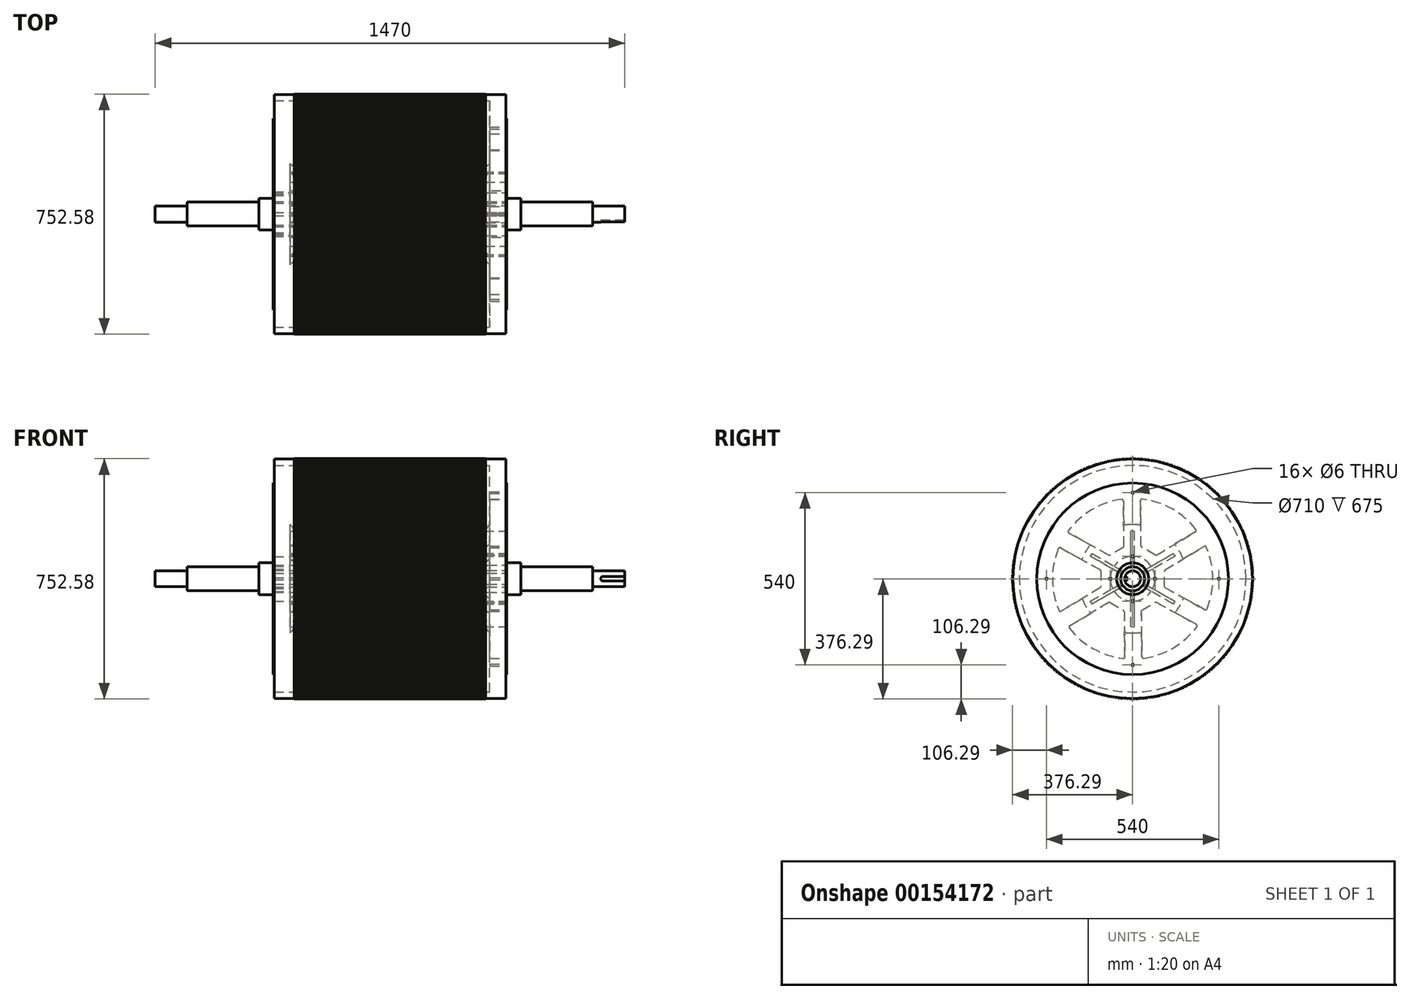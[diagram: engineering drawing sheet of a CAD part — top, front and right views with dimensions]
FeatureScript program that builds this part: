
annotation { "Feature Type Name" : "Feature", "Feature Type Description" : "" }
export const myFeature = defineFeature(function(context is Context, id is Id, definition is map)
    precondition{}
    {
        {
            var Q0;
            Q0=qCreatedBy(makeId("Front.planeOp"),FACE);
            var sketch = newSketch(context, id + "F0", { "sketchPlane" : qUnion([Q0])});
            skLineSegment(sketch, "E0", {"start": v(-128.4, 0) * mm, "end": v(171.6, 0) * mm, "construction": true});
            skLineSegment(sketch, "E1", {"start": v(0, 0) * mm, "end": v(362.5, 0) * mm});
            skLineSegment(sketch, "E2", {"start": v(0, 0) * mm, "end": v(-362.5, 0) * mm});
            skLineSegment(sketch, "E3", {"start": v(-362.5, 0) * mm, "end": v(-362.5, 375) * mm});
            skLineSegment(sketch, "E4", {"start": v(362.5, 375) * mm, "end": v(362.5, 0) * mm});
            skLineSegment(sketch, "E5.0", {"start": v(312.5, 355) * mm, "end": v(312.5, 70) * mm});
            skLineSegment(sketch, "E6", {"start": v(-312.5, 0) * mm, "end": v(-362.5, 0) * mm});
            skLineSegment(sketch, "E7", {"start": v(-362.5, 0) * mm, "end": v(-212.5, 0) * mm});
            skLineSegment(sketch, "E8", {"start": v(-212.5, 0) * mm, "end": v(-212.5, 70) * mm});
            skLineSegment(sketch, "E9", {"start": v(-212.5, 70) * mm, "end": v(-362.5, 70) * mm});
            skLineSegment(sketch, "E10.0", {"start": v(-212.5, 50) * mm, "end": v(-362.5, 50) * mm});
            skLineSegment(sketch, "E11", {"start": v(-362.5, 70) * mm, "end": v(-362.5, 50) * mm});
            skLineSegment(sketch, "E12", {"start": v(-212.5, 70) * mm, "end": v(-212.5, 50) * mm});
            skLineSegment(sketch, "E13", {"start": v(0, -51.64) * mm, "end": v(0, 29.66) * mm, "construction": true});
            skLineSegment(sketch, "E14", {"start": v(362.5, 0) * mm, "end": v(312.5, 0) * mm});
            skLineSegment(sketch, "E15", {"start": v(362.5, 0) * mm, "end": v(212.5, 0) * mm});
            skLineSegment(sketch, "E16", {"start": v(212.5, 0) * mm, "end": v(212.5, 70) * mm});
            skLineSegment(sketch, "E17", {"start": v(212.5, 70) * mm, "end": v(362.5, 70) * mm});
            skLineSegment(sketch, "E18.0", {"start": v(212.5, 50) * mm, "end": v(362.5, 50) * mm});
            skLineSegment(sketch, "E19", {"start": v(362.5, 70) * mm, "end": v(362.5, 50) * mm});
            skPoint(sketch, "E20", {"position": v(222.5, 170) * mm});
            skLineSegment(sketch, "E21", {"start": v(222.5, 170) * mm, "end": v(312.5, 170) * mm, "construction": true});
            skLineSegment(sketch, "E22", {"start": v(222.5, 170) * mm, "end": v(222.5, 70) * mm, "construction": true});
            skLineSegment(sketch, "E23", {"start": v(222.5, 70) * mm, "end": v(312.5, 170) * mm});
            skLineSegment(sketch, "E24.trimOffspring", {"start": v(-312.5, 70) * mm, "end": v(-312.5, 355) * mm});
            skPoint(sketch, "E25", {"position": v(-222.5, 170) * mm});
            skLineSegment(sketch, "E26", {"start": v(-222.5, 170) * mm, "end": v(-222.5, 70) * mm, "construction": true});
            skLineSegment(sketch, "E27", {"start": v(-222.5, 170) * mm, "end": v(-312.5, 170) * mm, "construction": true});
            skLineSegment(sketch, "E28", {"start": v(-222.5, 70) * mm, "end": v(-312.5, 170) * mm});
            skLineSegment(sketch, "E29", {"start": v(-362.5, 50) * mm, "end": v(-410, 50) * mm});
            skLineSegment(sketch, "E30", {"start": v(-410, 50) * mm, "end": v(-410, 42.5) * mm});
            skLineSegment(sketch, "E31", {"start": v(-410, 50) * mm, "end": v(-240, 50) * mm});
            skLineSegment(sketch, "E32", {"start": v(-240, 50) * mm, "end": v(-240, 0) * mm});
            skLineSegment(sketch, "E33", {"start": v(-410, 0) * mm, "end": v(-635, 0) * mm});
            skLineSegment(sketch, "E34", {"start": v(-362.5, 0) * mm, "end": v(-410, 0) * mm});
            skLineSegment(sketch, "E35", {"start": v(-635, 30) * mm, "end": v(-635, 37.5) * mm});
            skLineSegment(sketch, "E36", {"start": v(-635, 37.5) * mm, "end": v(-415, 37.5) * mm});
            skPoint(sketch, "E37.visualSharp", {"position": v(-410, 37.5) * mm});
            skArc(sketch, "E37.filletArc", {"start": v(-415, 37.5) * mm, "mid": v(-411.46, 38.96) * mm, "end": v(-410, 42.5) * mm});
            skLineSegment(sketch, "E38", {"start": v(362.5, 50) * mm, "end": v(410, 50) * mm});
            skLineSegment(sketch, "E39", {"start": v(410, 50) * mm, "end": v(410, 42.5) * mm});
            skLineSegment(sketch, "E40", {"start": v(410, 0) * mm, "end": v(362.5, 0) * mm});
            skLineSegment(sketch, "E41", {"start": v(410, 0) * mm, "end": v(635, 0) * mm});
            skLineSegment(sketch, "E42", {"start": v(635, 30) * mm, "end": v(635, 37.5) * mm});
            skLineSegment(sketch, "E43", {"start": v(635, 37.5) * mm, "end": v(415, 37.5) * mm});
            skPoint(sketch, "E44.visualSharp", {"position": v(410, 37.5) * mm});
            skArc(sketch, "E44.filletArc", {"start": v(410, 42.5) * mm, "mid": v(411.46, 38.96) * mm, "end": v(415, 37.5) * mm});
            skLineSegment(sketch, "E45", {"start": v(635, 0) * mm, "end": v(735, 0) * mm});
            skLineSegment(sketch, "E46", {"start": v(735, 0) * mm, "end": v(735, 25) * mm});
            skLineSegment(sketch, "E47", {"start": v(735, 25) * mm, "end": v(640, 25) * mm});
            skPoint(sketch, "E48.visualSharp", {"position": v(635, 25) * mm});
            skArc(sketch, "E48.filletArc", {"start": v(635, 30) * mm, "mid": v(636.46, 26.46) * mm, "end": v(640, 25) * mm});
            skLineSegment(sketch, "E49", {"start": v(735, 0) * mm, "end": v(660, 0) * mm});
            skLineSegment(sketch, "E50", {"start": v(660, 0) * mm, "end": v(660, 0) * mm});
            skLineSegment(sketch, "E51", {"start": v(-362.5, 50) * mm, "end": v(-362.5, 300) * mm});
            skLineSegment(sketch, "E52", {"start": v(-362.5, 300) * mm, "end": v(-365.5, 300) * mm});
            skLineSegment(sketch, "E53", {"start": v(-365.5, 300) * mm, "end": v(-365.5, 50) * mm});
            skLineSegment(sketch, "E54", {"start": v(362.5, 50) * mm, "end": v(362.5, 300) * mm});
            skLineSegment(sketch, "E55", {"start": v(362.5, 300) * mm, "end": v(365.5, 300) * mm});
            skLineSegment(sketch, "E56", {"start": v(365.5, 300) * mm, "end": v(365.5, 50) * mm});
            skLineSegment(sketch, "E57", {"start": v(-362.5, 375) * mm, "end": v(362.5, 375) * mm});
            skLineSegment(sketch, "E58.0", {"start": v(-362.5, 355) * mm, "end": v(362.5, 355) * mm});
            skLineSegment(sketch, "E59", {"start": v(-635, 0) * mm, "end": v(-735, 0) * mm});
            skLineSegment(sketch, "E60", {"start": v(-735, 0) * mm, "end": v(-735, 25) * mm});
            skLineSegment(sketch, "E61", {"start": v(-735, 25) * mm, "end": v(-640, 25) * mm});
            skPoint(sketch, "E62.visualSharp", {"position": v(-635, 25) * mm});
            skArc(sketch, "E62.filletArc", {"start": v(-640, 25) * mm, "mid": v(-636.46, 26.46) * mm, "end": v(-635, 30) * mm});
            skSolve(sketch);
        }
        {
            var Q0;
            {var subQ0=sQuery(id+"F0.wireOp",EDGE,"E30");Q0=makeQuery(id+"F0.imprint","IMPRINT",FACE,{"disambiguationData":[TD([[makeQuery(id+"F0.imprint","IMPRINT",EDGE,{"derivedFrom":subQ0}),1.0]])]});}
            var Q1;
            {var subQ0=sQuery(id+"F0.wireOp",EDGE,"E52");Q1=makeQuery(id+"F0.imprint","IMPRINT",FACE,{"disambiguationData":[TD([[makeQuery(id+"F0.imprint","IMPRINT",EDGE,{"derivedFrom":subQ0}),1.0]])]});}
            var Q2;
            {var subQ5=sQuery(id+"F0.wireOp",EDGE,"E32");Q2=makeQuery(id+"F0.imprint","IMPRINT",FACE,{"disambiguationData":[TD([[makeQuery(id+"F0.imprint","IMPRINT",EDGE,{"derivedFrom":subQ5}),-1.0]])]});}
            var Q3;
            {var subQ0=sQuery(id+"F0.wireOp",EDGE,"E8");Q3=makeQuery(id+"F0.imprint","IMPRINT",FACE,{"disambiguationData":[TD([[makeQuery(id+"F0.imprint","IMPRINT",EDGE,{"derivedFrom":subQ0}),1.0]])]});}
            var Q4;
            {var subQ0=sQuery(id+"F0.wireOp",EDGE,"E10.0");Q4=makeQuery(id+"F0.imprint","IMPRINT",FACE,{"disambiguationData":[TD([[makeQuery(id+"F0.imprint","IMPRINT",EDGE,{"derivedFrom":subQ0}),-1.0]])]});}
            var Q5;
            {var subQ3=sQuery(id+"F0.wireOp",EDGE,"E28");Q5=makeQuery(id+"F0.imprint","IMPRINT",FACE,{"disambiguationData":[TD([[makeQuery(id+"F0.imprint","IMPRINT",EDGE,{"derivedFrom":subQ3}),1.0]])]});}
            var Q6;
            {var subQ1=sQuery(id+"F0.wireOp",EDGE,"E9");var subQ4=sQuery(id+"F0.wireOp",EDGE,"E51");var subQ5=makeQuery(id+"F0.imprint","INTERSECT",VERTEX,{"derivedFrom":[subQ1,subQ4]});Q6=makeQuery(id+"F0.imprint","IMPRINT",FACE,{"disambiguationData":[TD([[makeQuery(id+"F0.imprint","IMPRINT",EDGE,{"disambiguationData":[TD([[subQ5,1.0]])],"derivedFrom":subQ1}),-1.0]])]});}
            var Q7;
            {var subQ4=sQuery(id+"F0.wireOp",EDGE,"E57");Q7=makeQuery(id+"F0.imprint","IMPRINT",FACE,{"disambiguationData":[TD([[makeQuery(id+"F0.imprint","IMPRINT",EDGE,{"derivedFrom":subQ4}),-1.0]])]});}
            var Q8;
            {var subQ1=sQuery(id+"F0.wireOp",EDGE,"E5.0");var subQ6=sQuery(id+"F0.wireOp",EDGE,"E58.0");var subQ7=makeQuery(id+"F0.imprint","INTERSECT",VERTEX,{"derivedFrom":[subQ1,subQ6]});Q8=makeQuery(id+"F0.imprint","IMPRINT",FACE,{"disambiguationData":[TD([[makeQuery(id+"F0.imprint","IMPRINT",EDGE,{"disambiguationData":[TD([[subQ7,-1.0]])],"derivedFrom":subQ1}),1.0]])]});}
            var Q9;
            {var subQ3=sQuery(id+"F0.wireOp",EDGE,"E23");Q9=makeQuery(id+"F0.imprint","IMPRINT",FACE,{"disambiguationData":[TD([[makeQuery(id+"F0.imprint","IMPRINT",EDGE,{"derivedFrom":subQ3}),-1.0]])]});}
            var Q10;
            {var subQ3=sQuery(id+"F0.wireOp",EDGE,"E18.0");Q10=makeQuery(id+"F0.imprint","IMPRINT",FACE,{"disambiguationData":[TD([[makeQuery(id+"F0.imprint","IMPRINT",EDGE,{"derivedFrom":subQ3}),-1.0]])]});}
            var Q11;
            {var subQ7=sQuery(id+"F0.wireOp",EDGE,"E18.0");Q11=makeQuery(id+"F0.imprint","IMPRINT",FACE,{"disambiguationData":[TD([[makeQuery(id+"F0.imprint","IMPRINT",EDGE,{"derivedFrom":subQ7}),1.0]])]});}
            var Q12;
            {var subQ4=sQuery(id+"F0.wireOp",EDGE,"E39");Q12=makeQuery(id+"F0.imprint","IMPRINT",FACE,{"disambiguationData":[TD([[makeQuery(id+"F0.imprint","IMPRINT",EDGE,{"derivedFrom":subQ4}),-1.0]])]});}
            var Q13;
            {var subQ0=sQuery(id+"F0.wireOp",EDGE,"E55");Q13=makeQuery(id+"F0.imprint","IMPRINT",FACE,{"disambiguationData":[TD([[makeQuery(id+"F0.imprint","IMPRINT",EDGE,{"derivedFrom":subQ0}),-1.0]])]});}
            var Q14;
            Q14=sQuery(id+"F0.wireOp",EDGE,"E2");
            revolve(context, id + "F1", {"entities" : qUnion([Q0, Q1, Q2, Q3, Q4, Q5, Q6, Q7, Q8, Q9, Q10, Q11, Q12, Q13]), "axis" : qUnion([Q14]), "revolveType" : RevolveType.FULL});
        }
        {
            var Q0;
            Q0=qCreatedBy(makeId("Right.planeOp"),FACE);
            cPlane(context, id + "F2", {"entities" : qUnion([Q0]), "cplaneType" : CPlaneType.OFFSET, "offset" : 362.5 * mm, "width" : 150 * mm, "height" : 150 * mm});
        }
        {
            var Q0;
            Q0=qCreatedBy(id+"F2.planeOp",FACE);
            var sketch = newSketch(context, id + "F3", { "sketchPlane" : qUnion([Q0])});
            skLineSegment(sketch, "E63", {"start": v(0, 0) * mm, "end": v(100, 0) * mm});
            skLineSegment(sketch, "E64", {"start": v(100, 0) * mm, "end": v(100, 24.17) * mm});
            skLineSegment(sketch, "E65", {"start": v(100, 0) * mm, "end": v(100, -24.06) * mm});
            skLineSegment(sketch, "E66", {"start": v(102.43, 28.46) * mm, "end": v(223.77, 101.26) * mm});
            skLineSegment(sketch, "E67", {"start": v(102.57, -28.43) * mm, "end": v(225.8, -96.84) * mm});
            skArc(sketch, "E68", {"start": v(230.94, 98.94) * mm, "mid": v(251.23, 2.49) * mm, "end": v(232.85, -94.34) * mm});
            skPoint(sketch, "E69.visualSharp", {"position": v(228.63, 104.17) * mm});
            skArc(sketch, "E69.filletArc", {"start": v(230.94, 98.94) * mm, "mid": v(227.88, 101.73) * mm, "end": v(223.77, 101.26) * mm});
            skPoint(sketch, "E70.newPointA", {"position": v(231.14, -99.8) * mm});
            skArc(sketch, "E70.filletArc", {"start": v(225.8, -96.84) * mm, "mid": v(229.88, -97.18) * mm, "end": v(232.85, -94.34) * mm});
            skPoint(sketch, "E71.visualSharp", {"position": v(100, 27) * mm});
            skArc(sketch, "E71.filletArc", {"start": v(102.43, 28.46) * mm, "mid": v(100.65, 26.63) * mm, "end": v(100, 24.17) * mm});
            skPoint(sketch, "E72.visualSharp", {"position": v(100, -27) * mm});
            skArc(sketch, "E72.filletArc", {"start": v(100, -24.06) * mm, "mid": v(100.7, -26.6) * mm, "end": v(102.57, -28.43) * mm});
            skArc(sketch, "E73.1.0", {"start": v(29.79, 249.47) * mm, "mid": v(123.46, 218.81) * mm, "end": v(198.13, 154.48) * mm});
            skArc(sketch, "E73.1.1", {"start": v(29.79, 249.47) * mm, "mid": v(25.84, 248.21) * mm, "end": v(24.2, 244.42) * mm});
            skLineSegment(sketch, "E73.1.2", {"start": v(26.57, 102.93) * mm, "end": v(24.2, 244.42) * mm});
            skLineSegment(sketch, "E73.1.3", {"start": v(50, 86.6) * mm, "end": v(29.07, 98.69) * mm});
            skArc(sketch, "E73.1.4", {"start": v(26.57, 102.93) * mm, "mid": v(27.26, 100.48) * mm, "end": v(29.07, 98.69) * mm});
            skLineSegment(sketch, "E73.1.5", {"start": v(50, 86.6) * mm, "end": v(70.83, 74.57) * mm});
            skArc(sketch, "E73.1.6", {"start": v(70.83, 74.57) * mm, "mid": v(73.38, 73.9) * mm, "end": v(75.9, 74.62) * mm});
            skLineSegment(sketch, "E73.1.7", {"start": v(75.9, 74.62) * mm, "end": v(196.76, 147.12) * mm});
            skArc(sketch, "E73.1.8", {"start": v(196.76, 147.12) * mm, "mid": v(199.1, 150.5) * mm, "end": v(198.13, 154.48) * mm});
            skArc(sketch, "E73.2.0", {"start": v(-201.15, 150.53) * mm, "mid": v(-127.77, 216.33) * mm, "end": v(-34.72, 248.83) * mm});
            skArc(sketch, "E73.2.1", {"start": v(-201.15, 150.53) * mm, "mid": v(-202.04, 146.49) * mm, "end": v(-199.58, 143.16) * mm});
            skLineSegment(sketch, "E73.2.2", {"start": v(-75.86, 74.48) * mm, "end": v(-199.58, 143.16) * mm});
            skLineSegment(sketch, "E73.2.3", {"start": v(-50, 86.6) * mm, "end": v(-70.93, 74.52) * mm});
            skArc(sketch, "E73.2.4", {"start": v(-75.86, 74.48) * mm, "mid": v(-73.39, 73.85) * mm, "end": v(-70.93, 74.52) * mm});
            skLineSegment(sketch, "E73.2.5", {"start": v(-50, 86.6) * mm, "end": v(-29.17, 98.63) * mm});
            skArc(sketch, "E73.2.6", {"start": v(-29.17, 98.63) * mm, "mid": v(-27.32, 100.5) * mm, "end": v(-26.67, 103.05) * mm});
            skLineSegment(sketch, "E73.2.7", {"start": v(-26.67, 103.05) * mm, "end": v(-29.03, 243.96) * mm});
            skArc(sketch, "E73.2.8", {"start": v(-29.03, 243.96) * mm, "mid": v(-30.78, 247.68) * mm, "end": v(-34.72, 248.83) * mm});
            skArc(sketch, "E73.3.0", {"start": v(-230.94, -98.94) * mm, "mid": v(-251.23, -2.49) * mm, "end": v(-232.85, 94.34) * mm});
            skArc(sketch, "E73.3.1", {"start": v(-230.94, -98.94) * mm, "mid": v(-227.88, -101.73) * mm, "end": v(-223.77, -101.26) * mm});
            skLineSegment(sketch, "E73.3.2", {"start": v(-102.43, -28.46) * mm, "end": v(-223.77, -101.26) * mm});
            skLineSegment(sketch, "E73.3.3", {"start": v(-100, 0) * mm, "end": v(-100, -24.17) * mm});
            skArc(sketch, "E73.3.4", {"start": v(-102.43, -28.46) * mm, "mid": v(-100.65, -26.63) * mm, "end": v(-100, -24.17) * mm});
            skLineSegment(sketch, "E73.3.5", {"start": v(-100, 0) * mm, "end": v(-100, 24.06) * mm});
            skArc(sketch, "E73.3.6", {"start": v(-100, 24.06) * mm, "mid": v(-100.7, 26.6) * mm, "end": v(-102.57, 28.43) * mm});
            skLineSegment(sketch, "E73.3.7", {"start": v(-102.57, 28.43) * mm, "end": v(-225.8, 96.84) * mm});
            skArc(sketch, "E73.3.8", {"start": v(-225.8, 96.84) * mm, "mid": v(-229.88, 97.18) * mm, "end": v(-232.85, 94.34) * mm});
            skArc(sketch, "E73.4.0", {"start": v(-29.79, -249.47) * mm, "mid": v(-123.46, -218.81) * mm, "end": v(-198.13, -154.48) * mm});
            skArc(sketch, "E73.4.1", {"start": v(-29.79, -249.47) * mm, "mid": v(-25.84, -248.21) * mm, "end": v(-24.2, -244.42) * mm});
            skLineSegment(sketch, "E73.4.2", {"start": v(-26.57, -102.93) * mm, "end": v(-24.2, -244.42) * mm});
            skLineSegment(sketch, "E73.4.3", {"start": v(-50, -86.6) * mm, "end": v(-29.07, -98.69) * mm});
            skArc(sketch, "E73.4.4", {"start": v(-26.57, -102.93) * mm, "mid": v(-27.26, -100.48) * mm, "end": v(-29.07, -98.69) * mm});
            skLineSegment(sketch, "E73.4.5", {"start": v(-50, -86.6) * mm, "end": v(-70.83, -74.57) * mm});
            skArc(sketch, "E73.4.6", {"start": v(-70.83, -74.57) * mm, "mid": v(-73.38, -73.9) * mm, "end": v(-75.9, -74.62) * mm});
            skLineSegment(sketch, "E73.4.7", {"start": v(-75.9, -74.62) * mm, "end": v(-196.76, -147.12) * mm});
            skArc(sketch, "E73.4.8", {"start": v(-196.76, -147.12) * mm, "mid": v(-199.1, -150.5) * mm, "end": v(-198.13, -154.48) * mm});
            skArc(sketch, "E73.5.0", {"start": v(201.15, -150.53) * mm, "mid": v(127.77, -216.33) * mm, "end": v(34.72, -248.83) * mm});
            skArc(sketch, "E73.5.1", {"start": v(201.15, -150.53) * mm, "mid": v(202.04, -146.49) * mm, "end": v(199.58, -143.16) * mm});
            skLineSegment(sketch, "E73.5.2", {"start": v(75.86, -74.48) * mm, "end": v(199.58, -143.16) * mm});
            skLineSegment(sketch, "E73.5.3", {"start": v(50, -86.6) * mm, "end": v(70.93, -74.52) * mm});
            skArc(sketch, "E73.5.4", {"start": v(75.86, -74.48) * mm, "mid": v(73.39, -73.85) * mm, "end": v(70.93, -74.52) * mm});
            skLineSegment(sketch, "E73.5.5", {"start": v(50, -86.6) * mm, "end": v(29.17, -98.63) * mm});
            skArc(sketch, "E73.5.6", {"start": v(29.17, -98.63) * mm, "mid": v(27.32, -100.5) * mm, "end": v(26.67, -103.05) * mm});
            skLineSegment(sketch, "E73.5.7", {"start": v(26.67, -103.05) * mm, "end": v(29.03, -243.96) * mm});
            skArc(sketch, "E73.5.8", {"start": v(29.03, -243.96) * mm, "mid": v(30.78, -247.68) * mm, "end": v(34.72, -248.83) * mm});
            skLineSegment(sketch, "E74", {"start": v(0, 0) * mm, "end": v(0, 150) * mm});
            skLineSegment(sketch, "E75", {"start": v(0, 150) * mm, "end": v(-5, 149.92) * mm});
            skLineSegment(sketch, "E76", {"start": v(0, 150) * mm, "end": v(5, 149.96) * mm});
            skPoint(sketch, "E76.endSnap0", {"position": v(-2.5, 149.96) * mm});
            skLineSegment(sketch, "E77", {"start": v(0, 0) * mm, "end": v(0, 42.5) * mm});
            skLineSegment(sketch, "E78", {"start": v(5, 149.96) * mm, "end": v(5, 42.5) * mm});
            skLineSegment(sketch, "E79", {"start": v(5, 42.5) * mm, "end": v(-5, 42.5) * mm});
            skLineSegment(sketch, "E80", {"start": v(-5, 42.5) * mm, "end": v(-5, 149.92) * mm});
            skLineSegment(sketch, "E81.1.0", {"start": v(-127.37, 79.3) * mm, "end": v(-34.3, 25.58) * mm});
            skLineSegment(sketch, "E81.1.1", {"start": v(-39.3, 16.92) * mm, "end": v(-132.33, 70.63) * mm});
            skLineSegment(sketch, "E81.1.2", {"start": v(-129.9, 75) * mm, "end": v(-127.37, 79.3) * mm});
            skLineSegment(sketch, "E81.1.3", {"start": v(-129.9, 75) * mm, "end": v(-132.33, 70.63) * mm});
            skLineSegment(sketch, "E81.1.4", {"start": v(-34.3, 25.58) * mm, "end": v(-39.3, 16.92) * mm});
            skLineSegment(sketch, "E81.2.0", {"start": v(-132.37, -70.65) * mm, "end": v(-39.3, -16.92) * mm});
            skLineSegment(sketch, "E81.2.1", {"start": v(-34.3, -25.58) * mm, "end": v(-127.33, -79.29) * mm});
            skLineSegment(sketch, "E81.2.2", {"start": v(-129.9, -75) * mm, "end": v(-132.37, -70.65) * mm});
            skLineSegment(sketch, "E81.2.3", {"start": v(-129.9, -75) * mm, "end": v(-127.33, -79.29) * mm});
            skLineSegment(sketch, "E81.2.4", {"start": v(-39.3, -16.92) * mm, "end": v(-34.3, -25.58) * mm});
            skLineSegment(sketch, "E81.3.0", {"start": v(-5, -149.96) * mm, "end": v(-5, -42.5) * mm});
            skLineSegment(sketch, "E81.3.1", {"start": v(5, -42.5) * mm, "end": v(5, -149.92) * mm});
            skLineSegment(sketch, "E81.3.2", {"start": v(0, -150) * mm, "end": v(-5, -149.96) * mm});
            skLineSegment(sketch, "E81.3.3", {"start": v(0, -150) * mm, "end": v(5, -149.92) * mm});
            skLineSegment(sketch, "E81.3.4", {"start": v(-5, -42.5) * mm, "end": v(5, -42.5) * mm});
            skLineSegment(sketch, "E81.4.0", {"start": v(127.37, -79.3) * mm, "end": v(34.3, -25.58) * mm});
            skLineSegment(sketch, "E81.4.1", {"start": v(39.3, -16.92) * mm, "end": v(132.33, -70.63) * mm});
            skLineSegment(sketch, "E81.4.2", {"start": v(129.9, -75) * mm, "end": v(127.37, -79.3) * mm});
            skLineSegment(sketch, "E81.4.3", {"start": v(129.9, -75) * mm, "end": v(132.33, -70.63) * mm});
            skLineSegment(sketch, "E81.4.4", {"start": v(34.3, -25.58) * mm, "end": v(39.3, -16.92) * mm});
            skLineSegment(sketch, "E81.5.0", {"start": v(132.37, 70.65) * mm, "end": v(39.3, 16.92) * mm});
            skLineSegment(sketch, "E81.5.1", {"start": v(34.3, 25.58) * mm, "end": v(127.33, 79.29) * mm});
            skLineSegment(sketch, "E81.5.2", {"start": v(129.9, 75) * mm, "end": v(132.37, 70.65) * mm});
            skLineSegment(sketch, "E81.5.3", {"start": v(129.9, 75) * mm, "end": v(127.33, 79.29) * mm});
            skLineSegment(sketch, "E81.5.4", {"start": v(39.3, 16.92) * mm, "end": v(34.3, 25.58) * mm});
            skSolve(sketch);
        }
        {
            var Q0;
            Q0=qSketchRegion(id+"F3",true);
            extrude(context, id + "F4", {"entities" : qUnion([Q0]), "operationType" : NewBodyOperationType.REMOVE, "oppositeDirection" : true, "depth" : 725 * mm});
        }
        {
            var Q0;
            Q0=qCreatedBy(makeId("Front.planeOp"),FACE);
            cPlane(context, id + "F5", {"entities" : qUnion([Q0]), "cplaneType" : CPlaneType.OFFSET, "offset" : 25 * mm, "width" : 150 * mm, "height" : 150 * mm});
        }
        {
            var Q0;
            Q0=qCreatedBy(id+"F5.planeOp",FACE);
            var sketch = newSketch(context, id + "F6", { "sketchPlane" : qUnion([Q0])});
            skLineSegment(sketch, "E82.0", {"start": v(735, -25) * mm, "end": v(735, 25) * mm});
            skLineSegment(sketch, "E83", {"start": v(735, -25) * mm, "end": v(735, 0) * mm});
            skLineSegment(sketch, "E84", {"start": v(735, 0) * mm, "end": v(697.5, 0) * mm});
            skLineSegment(sketch, "E85.left", {"start": v(735, 7) * mm, "end": v(735, -7) * mm});
            skPoint(sketch, "E85.middle", {"position": v(697.5, 0) * mm});
            skLineSegment(sketch, "E86.bottom", {"start": v(735, 7) * mm, "end": v(667, 7) * mm});
            skLineSegment(sketch, "E86.top", {"start": v(735, -7) * mm, "end": v(667, -7) * mm});
            skLineSegment(sketch, "E86.right", {"start": v(660, 0) * mm, "end": v(660, 0) * mm});
            skPoint(sketch, "E87.visualSharp", {"position": v(660, 7) * mm});
            skArc(sketch, "E87.filletArc", {"start": v(667, 7) * mm, "mid": v(662.05, 4.95) * mm, "end": v(660, 0) * mm});
            skPoint(sketch, "E88.visualSharp", {"position": v(660, -7) * mm});
            skArc(sketch, "E88.filletArc", {"start": v(660, 0) * mm, "mid": v(662.05, -4.95) * mm, "end": v(667, -7) * mm});
            skSolve(sketch);
        }
        {
            var Q0;
            Q0=qSketchRegion(id+"F6",true);
            extrude(context, id + "F7", {"entities" : qUnion([Q0]), "operationType" : NewBodyOperationType.REMOVE, "oppositeDirection" : true, "depth" : 6.5 * mm});
        }
        {
            var Q0;
            Q0=qCreatedBy(makeId("Right.planeOp"),FACE);
            cPlane(context, id + "F8", {"entities" : qUnion([Q0]), "cplaneType" : CPlaneType.OFFSET, "offset" : 300 * mm, "width" : 150 * mm, "height" : 150 * mm});
        }
        {
            var Q0;
            Q0=qCreatedBy(id+"F8.planeOp",FACE);
            var sketch = newSketch(context, id + "F9", { "sketchPlane" : qUnion([Q0])});
            skArc(sketch, "E89.0", {"start": v(-29.98, 373.8) * mm, "mid": v(-30.58, 373.75) * mm, "end": v(-31.18, 373.7) * mm});
            skLineSegment(sketch, "E90", {"start": v(-31.18, 373.7) * mm, "end": v(-31.18, 375) * mm});
            skLineSegment(sketch, "E91", {"start": v(-31.18, 375) * mm, "end": v(-29.98, 375) * mm});
            skLineSegment(sketch, "E92", {"start": v(-29.98, 375) * mm, "end": v(-29.98, 373.8) * mm});
            skSolve(sketch);
        }
        {
            var Q0;
            Q0=qSketchRegion(id+"F9",true);
            extrude(context, id + "F10", {"entities" : qUnion([Q0]), "oppositeDirection" : true, "depth" : 600 * mm});
        }
        {
            var Q0;
            Q0=makeQuery(id+"F10.opExtrude","SWEPT_BODY",BODY,{"disambiguationData":[OSD([sQuery(id+"F9.wireOp",EDGE,"E89.0"),sQuery(id+"F9.wireOp",EDGE,"E90"),sQuery(id+"F9.wireOp",EDGE,"E91"),sQuery(id+"F9.wireOp",EDGE,"E92")])]});
            var Q1;
            Q1=makeQuery(id+"F1.opRevolve","SWEPT_FACE",FACE,{"disambiguationData":[OSD([sQuery(id+"F0.wireOp",EDGE,"E57")])]});
            circularPattern(context, id + "F11", {"entities" : qUnion([Q0]), "axis" : qUnion([Q1]), "angle" : 0.5 * degree, "instanceCount" : 725});
        }
        {
            var Q0;
            Q0=makeQuery(id+"F1.opRevolve","SWEPT_FACE",FACE,{"disambiguationData":[OSD([sQuery(id+"F0.wireOp",EDGE,"E56")])]});
            var sketch = newSketch(context, id + "F12", { "sketchPlane" : qUnion([Q0])});
            skLineSegment(sketch, "E93", {"start": v(0, 0) * mm, "end": v(0, 270) * mm});
            skCircle(sketch, "E94", {"center": v(0, 270) * mm, "radius": 3 * mm});
            skPoint(sketch, "E95", {"position": v(270, 0) * mm});
            skPoint(sketch, "E96", {"position": v(0, 0) * mm});
            skPoint(sketch, "E97", {"position": v(-270, 0) * mm});
            skPoint(sketch, "E98", {"position": v(0, -270) * mm});
            skCircle(sketch, "E99", {"center": v(-270, 0) * mm, "radius": 3 * mm});
            skCircle(sketch, "E100", {"center": v(270, 0) * mm, "radius": 3 * mm});
            skCircle(sketch, "E101", {"center": v(0, -270) * mm, "radius": 3 * mm});
            skPoint(sketch, "E102", {"position": v(0, -70) * mm});
            skPoint(sketch, "E103", {"position": v(0, 70) * mm});
            skPoint(sketch, "E104", {"position": v(-70, 0) * mm});
            skPoint(sketch, "E105", {"position": v(70, 0) * mm});
            skCircle(sketch, "E106", {"center": v(0, 70) * mm, "radius": 3 * mm});
            skCircle(sketch, "E107", {"center": v(-70, 0) * mm, "radius": 3 * mm});
            skCircle(sketch, "E108", {"center": v(0, -70) * mm, "radius": 3 * mm});
            skCircle(sketch, "E109", {"center": v(70, 0) * mm, "radius": 3 * mm});
            skSolve(sketch);
        }
        {
            var Q0;
            Q0=qSketchRegion(id+"F12",true);
            extrude(context, id + "F13", {"entities" : qUnion([Q0]), "operationType" : NewBodyOperationType.REMOVE, "oppositeDirection" : true, "depth" : 731 * mm});
        }
    });
